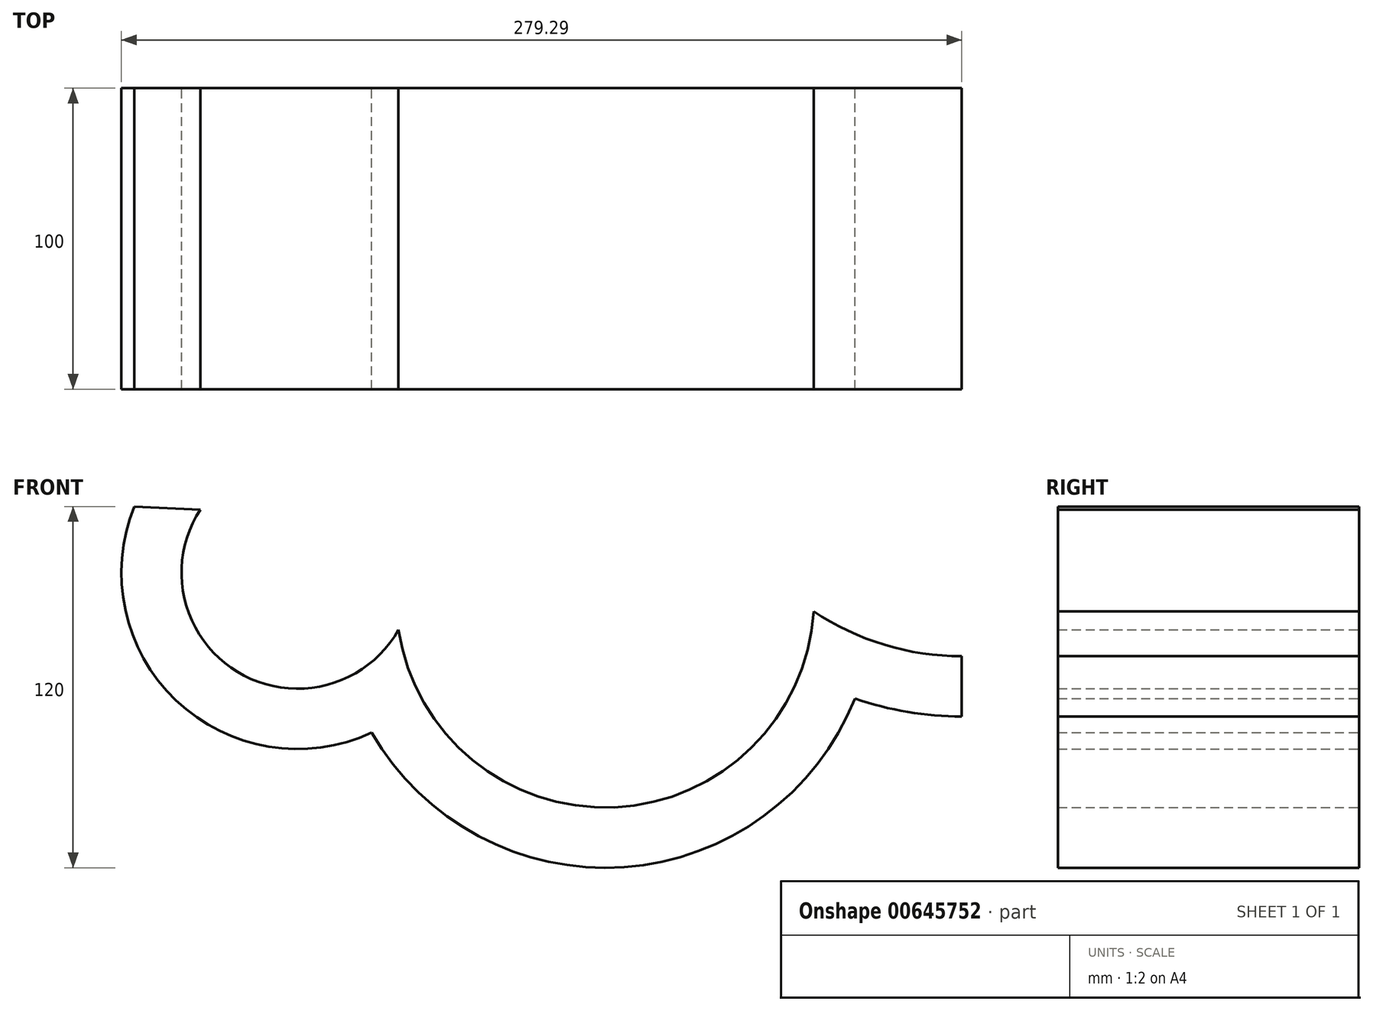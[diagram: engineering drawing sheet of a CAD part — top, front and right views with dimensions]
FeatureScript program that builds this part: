
annotation { "Feature Type Name" : "Feature", "Feature Type Description" : "" }
export const myFeature = defineFeature(function(context is Context, id is Id, definition is map)
    precondition{}
    {
        {
            var Q0;
            Q0=qCreatedBy(makeId("Front.planeOp"),FACE);
            var sketch = newSketch(context, id + "F0", { "sketchPlane" : qUnion([Q0])});
            skLineSegment(sketch, "E0", {"start": v(0, 270.7) * mm, "end": v(0, -251.2) * mm, "construction": true});
            skLineSegment(sketch, "E1", {"start": v(-134.26, -103.53) * mm, "end": v(109.58, -103.53) * mm, "construction": true});
            skArc(sketch, "E2", {"start": v(-275, 16.47) * mm, "mid": v(-261.1, -47.93) * mm, "end": v(-196.08, -58.6) * mm});
            skArc(sketch, "E3", {"start": v(-196.08, -58.6) * mm, "mid": v(-112.24, -103.3) * mm, "end": v(-35.49, -47.3) * mm});
            skArc(sketch, "E4.0", {"start": v(-253.07, 15.47) * mm, "mid": v(-240.71, -38.48) * mm, "end": v(-187.17, -24.44) * mm});
            skArc(sketch, "E5.0", {"start": v(-187.17, -24.44) * mm, "mid": v(-115.44, -83.46) * mm, "end": v(-49.22, -18.33) * mm});
            skLineSegment(sketch, "E6", {"start": v(-275, 16.47) * mm, "end": v(-253.07, 15.47) * mm});
            skPoint(sketch, "E7.orphan", {"position": v(44.09, 0) * mm});
            skPoint(sketch, "E8.orphan", {"position": v(-7.07, 0) * mm});
            skArc(sketch, "E9", {"start": v(-35.49, -47.3) * mm, "mid": v(-18, -51.77) * mm, "end": v(0, -53.27) * mm});
            skArc(sketch, "E10.0", {"start": v(-49.22, -18.33) * mm, "mid": v(-25.72, -29.46) * mm, "end": v(0, -33.27) * mm});
            skPoint(sketch, "E11.orphan", {"position": v(35.49, -47.3) * mm});
            skLineSegment(sketch, "E12", {"start": v(0, -53.27) * mm, "end": v(0, -33.27) * mm});
            skSolve(sketch);
        }
        {
            var Q0;
            Q0=qSketchRegion(id+"F0",true);
            extrude(context, id + "F1", {"entities" : qUnion([Q0]), "depth" : 100 * mm});
        }
    });
